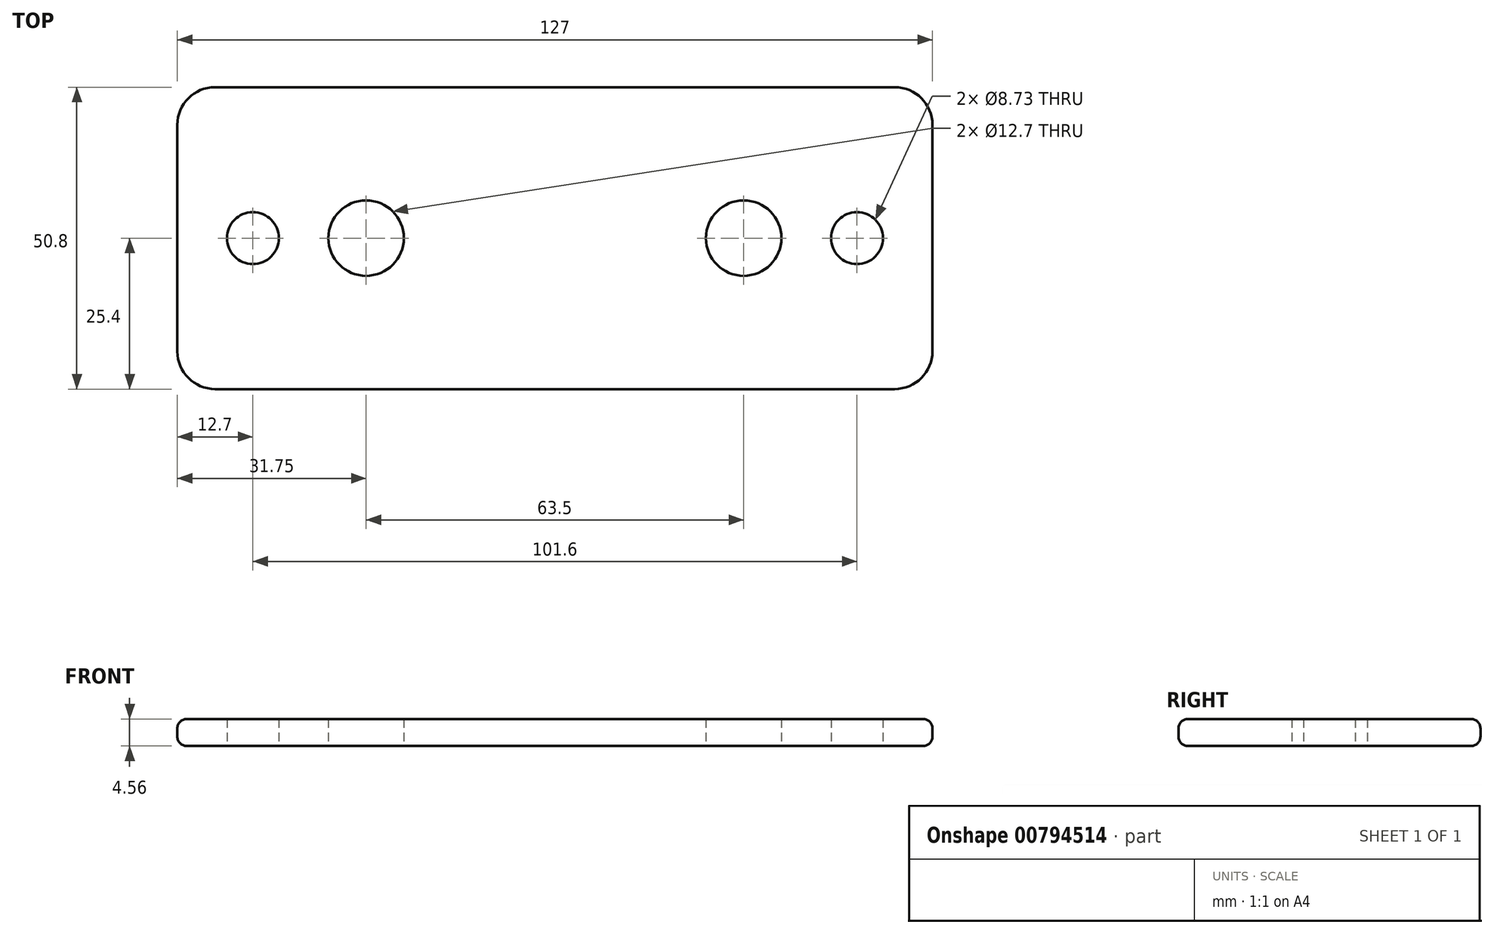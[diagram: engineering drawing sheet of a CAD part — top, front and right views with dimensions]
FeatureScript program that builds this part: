
annotation { "Feature Type Name" : "Feature", "Feature Type Description" : "" }
export const myFeature = defineFeature(function(context is Context, id is Id, definition is map)
    precondition{}
    {
        {
            var Q0;
            Q0=qCreatedBy(makeId("Top.planeOp"),FACE);
            var sketch = newSketch(context, id + "F0", { "sketchPlane" : qUnion([Q0])});
            skLineSegment(sketch, "E0.bottom", {"start": v(-57.15, 25.4) * mm, "end": v(57.15, 25.4) * mm});
            skLineSegment(sketch, "E0.top", {"start": v(-57.15, -25.4) * mm, "end": v(57.15, -25.4) * mm});
            skLineSegment(sketch, "E0.left", {"start": v(-63.5, 19.05) * mm, "end": v(-63.5, -19.05) * mm});
            skLineSegment(sketch, "E0.right", {"start": v(63.5, 19.05) * mm, "end": v(63.5, -19.05) * mm});
            skPoint(sketch, "E0.middle", {"position": v(0, 0) * mm});
            skCircle(sketch, "E1", {"center": v(-50.8, 0) * mm, "radius": 4.37 * mm});
            skCircle(sketch, "E2", {"center": v(50.8, 0) * mm, "radius": 4.37 * mm});
            skCircle(sketch, "E3", {"center": v(-31.75, 0) * mm, "radius": 6.35 * mm});
            skCircle(sketch, "E4", {"center": v(31.75, 0) * mm, "radius": 6.35 * mm});
            skPoint(sketch, "E5.visualSharp", {"position": v(-63.5, 25.4) * mm});
            skArc(sketch, "E5.filletArc", {"start": v(-57.15, 25.4) * mm, "mid": v(-61.64, 23.54) * mm, "end": v(-63.5, 19.05) * mm});
            skPoint(sketch, "E6.visualSharp", {"position": v(63.5, 25.4) * mm});
            skArc(sketch, "E6.filletArc", {"start": v(63.5, 19.05) * mm, "mid": v(61.64, 23.54) * mm, "end": v(57.15, 25.4) * mm});
            skPoint(sketch, "E7.visualSharp", {"position": v(63.5, -25.4) * mm});
            skArc(sketch, "E7.filletArc", {"start": v(57.15, -25.4) * mm, "mid": v(61.64, -23.54) * mm, "end": v(63.5, -19.05) * mm});
            skPoint(sketch, "E8.visualSharp", {"position": v(-63.5, -25.4) * mm});
            skArc(sketch, "E8.filletArc", {"start": v(-63.5, -19.05) * mm, "mid": v(-61.64, -23.54) * mm, "end": v(-57.15, -25.4) * mm});
            skSolve(sketch);
        }
        {
            var Q0;
            Q0=makeQuery(id+"F0.imprint","IMPRINT",FACE,{"disambiguationData":[TD([[makeQuery(id+"F0.imprint","IMPRINT",EDGE,{"derivedFrom":sQuery(id+"F0.wireOp",EDGE,"E0.bottom")}),-1.0]])]});
            extrude(context, id + "F1", {"entities" : qUnion([Q0]), "endBound" : BoundingType.SYMMETRIC, "depth" : 4.55 * mm, "offsetDistance" : 25.4 * mm});
        }
        {
            var Q0;
            Q0=makeQuery(id+"F1.opExtrude","CAP_EDGE",EDGE,{"disambiguationData":[OSD([sQuery(id+"F0.wireOp",EDGE,"E0.top")])],"isStart":false});
            var Q1;
            Q1=makeQuery(id+"F1.opExtrude","CAP_EDGE",EDGE,{"disambiguationData":[OSD([sQuery(id+"F0.wireOp",EDGE,"E0.top")])],"isStart":true});
            fillet(context, id + "F2", {"entities" : qUnion([Q0, Q1]), "radius" : 1.59 * mm, "tangentPropagation" : true, "allowEdgeOverflow" : false});
        }
    });
